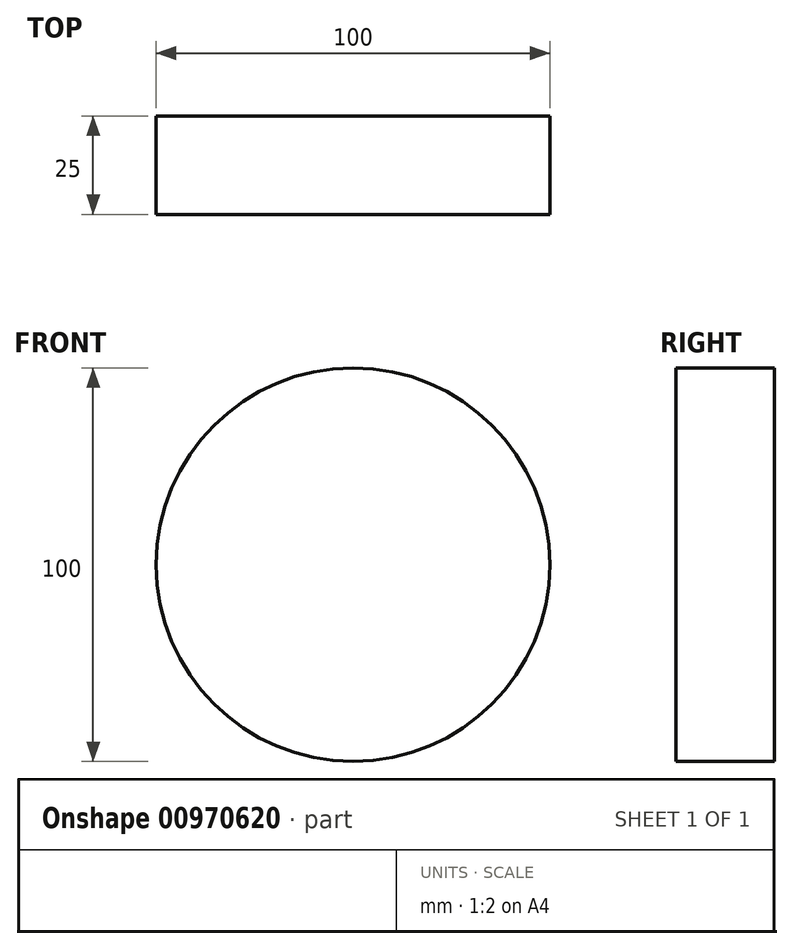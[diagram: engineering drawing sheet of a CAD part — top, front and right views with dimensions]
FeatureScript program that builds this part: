
annotation { "Feature Type Name" : "Feature", "Feature Type Description" : "" }
export const myFeature = defineFeature(function(context is Context, id is Id, definition is map)
    precondition{}
    {
        {
            var Q0;
            Q0=qCreatedBy(makeId("Front.planeOp"),FACE);
            var sketch = newSketch(context, id + "F0", { "sketchPlane" : qUnion([Q0])});
            skCircle(sketch, "E0", {"center": v(0, 0) * mm, "radius": 50 * mm});
            skLineSegment(sketch, "E1", {"start": v(-6.23, 49.61) * mm, "end": v(-1.88, 59.39) * mm});
            skLineSegment(sketch, "E2", {"start": v(-1.88, 59.39) * mm, "end": v(2.2, 59.39) * mm});
            skLineSegment(sketch, "E3", {"start": v(2.2, 59.39) * mm, "end": v(6.5, 49.57) * mm});
            skLineSegment(sketch, "E4.1.0", {"start": v(-22.08, 55.17) * mm, "end": v(-18.24, 56.56) * mm});
            skLineSegment(sketch, "E4.1.1", {"start": v(-18.24, 56.56) * mm, "end": v(-10.84, 48.81) * mm});
            skLineSegment(sketch, "E4.1.2", {"start": v(-22.82, 44.49) * mm, "end": v(-22.08, 55.17) * mm});
            skLineSegment(sketch, "E4.2.0", {"start": v(-39.61, 44.29) * mm, "end": v(-36.49, 46.91) * mm});
            skLineSegment(sketch, "E4.2.1", {"start": v(-36.49, 46.91) * mm, "end": v(-26.88, 42.16) * mm});
            skLineSegment(sketch, "E4.2.2", {"start": v(-36.66, 34) * mm, "end": v(-39.61, 44.29) * mm});
            skLineSegment(sketch, "E4.3.0", {"start": v(-52.37, 28.07) * mm, "end": v(-50.33, 31.6) * mm});
            skLineSegment(sketch, "E4.3.1", {"start": v(-50.33, 31.6) * mm, "end": v(-39.68, 30.42) * mm});
            skLineSegment(sketch, "E4.3.2", {"start": v(-46.08, 19.41) * mm, "end": v(-52.37, 28.07) * mm});
            skLineSegment(sketch, "E4.4.0", {"start": v(-58.81, 8.46) * mm, "end": v(-58.1, 12.48) * mm});
            skLineSegment(sketch, "E4.4.1", {"start": v(-58.1, 12.48) * mm, "end": v(-47.7, 15.02) * mm});
            skLineSegment(sketch, "E4.4.2", {"start": v(-49.94, 2.48) * mm, "end": v(-58.81, 8.46) * mm});
            skLineSegment(sketch, "E4.5.0", {"start": v(-58.16, -12.16) * mm, "end": v(-58.87, -8.14) * mm});
            skLineSegment(sketch, "E4.5.1", {"start": v(-58.87, -8.14) * mm, "end": v(-49.95, -2.2) * mm});
            skLineSegment(sketch, "E4.5.2", {"start": v(-47.78, -14.75) * mm, "end": v(-58.16, -12.16) * mm});
            skLineSegment(sketch, "E4.6.0", {"start": v(-50.5, -31.32) * mm, "end": v(-52.54, -27.78) * mm});
            skLineSegment(sketch, "E4.6.1", {"start": v(-52.54, -27.78) * mm, "end": v(-46.19, -19.15) * mm});
            skLineSegment(sketch, "E4.6.2", {"start": v(-39.85, -30.2) * mm, "end": v(-50.5, -31.32) * mm});
            skLineSegment(sketch, "E4.7.0", {"start": v(-36.74, -46.7) * mm, "end": v(-39.86, -44.08) * mm});
            skLineSegment(sketch, "E4.7.1", {"start": v(-39.86, -44.08) * mm, "end": v(-36.85, -33.8) * mm});
            skLineSegment(sketch, "E4.7.2", {"start": v(-27.12, -42) * mm, "end": v(-36.74, -46.7) * mm});
            skLineSegment(sketch, "E4.8.0", {"start": v(-18.55, -56.45) * mm, "end": v(-22.38, -55.05) * mm});
            skLineSegment(sketch, "E4.8.1", {"start": v(-22.38, -55.05) * mm, "end": v(-23.07, -44.36) * mm});
            skLineSegment(sketch, "E4.8.2", {"start": v(-11.11, -48.75) * mm, "end": v(-18.55, -56.45) * mm});
            skLineSegment(sketch, "E4.9.0", {"start": v(1.88, -59.39) * mm, "end": v(-2.2, -59.39) * mm});
            skLineSegment(sketch, "E4.9.1", {"start": v(-2.2, -59.39) * mm, "end": v(-6.5, -49.57) * mm});
            skLineSegment(sketch, "E4.9.2", {"start": v(6.23, -49.61) * mm, "end": v(1.88, -59.39) * mm});
            skLineSegment(sketch, "E4.10.0", {"start": v(22.08, -55.17) * mm, "end": v(18.24, -56.56) * mm});
            skLineSegment(sketch, "E4.10.1", {"start": v(18.24, -56.56) * mm, "end": v(10.84, -48.81) * mm});
            skLineSegment(sketch, "E4.10.2", {"start": v(22.82, -44.49) * mm, "end": v(22.08, -55.17) * mm});
            skLineSegment(sketch, "E4.11.0", {"start": v(39.61, -44.29) * mm, "end": v(36.49, -46.91) * mm});
            skLineSegment(sketch, "E4.11.1", {"start": v(36.49, -46.91) * mm, "end": v(26.88, -42.16) * mm});
            skLineSegment(sketch, "E4.11.2", {"start": v(36.66, -34) * mm, "end": v(39.61, -44.29) * mm});
            skLineSegment(sketch, "E4.12.0", {"start": v(52.37, -28.07) * mm, "end": v(50.33, -31.6) * mm});
            skLineSegment(sketch, "E4.12.1", {"start": v(50.33, -31.6) * mm, "end": v(39.68, -30.42) * mm});
            skLineSegment(sketch, "E4.12.2", {"start": v(46.08, -19.41) * mm, "end": v(52.37, -28.07) * mm});
            skLineSegment(sketch, "E4.13.0", {"start": v(58.81, -8.46) * mm, "end": v(58.1, -12.48) * mm});
            skLineSegment(sketch, "E4.13.1", {"start": v(58.1, -12.48) * mm, "end": v(47.7, -15.02) * mm});
            skLineSegment(sketch, "E4.13.2", {"start": v(49.94, -2.48) * mm, "end": v(58.81, -8.46) * mm});
            skLineSegment(sketch, "E4.14.0", {"start": v(58.16, 12.16) * mm, "end": v(58.87, 8.14) * mm});
            skLineSegment(sketch, "E4.14.1", {"start": v(58.87, 8.14) * mm, "end": v(49.95, 2.2) * mm});
            skLineSegment(sketch, "E4.14.2", {"start": v(47.78, 14.75) * mm, "end": v(58.16, 12.16) * mm});
            skLineSegment(sketch, "E4.15.0", {"start": v(50.5, 31.32) * mm, "end": v(52.54, 27.78) * mm});
            skLineSegment(sketch, "E4.15.1", {"start": v(52.54, 27.78) * mm, "end": v(46.19, 19.15) * mm});
            skLineSegment(sketch, "E4.15.2", {"start": v(39.85, 30.2) * mm, "end": v(50.5, 31.32) * mm});
            skLineSegment(sketch, "E4.16.0", {"start": v(36.74, 46.7) * mm, "end": v(39.86, 44.08) * mm});
            skLineSegment(sketch, "E4.16.1", {"start": v(39.86, 44.08) * mm, "end": v(36.85, 33.8) * mm});
            skLineSegment(sketch, "E4.16.2", {"start": v(27.12, 42) * mm, "end": v(36.74, 46.7) * mm});
            skLineSegment(sketch, "E4.17.0", {"start": v(18.55, 56.45) * mm, "end": v(22.38, 55.05) * mm});
            skLineSegment(sketch, "E4.17.1", {"start": v(22.38, 55.05) * mm, "end": v(23.07, 44.36) * mm});
            skLineSegment(sketch, "E4.17.2", {"start": v(11.11, 48.75) * mm, "end": v(18.55, 56.45) * mm});
            skSolve(sketch);
        }
        {
            var Q0;
            {var subQ0=sQuery(id+"F0.wireOp",EDGE,"E0");var subQ18=makeQuery(id+"F0.imprint","INTERSECT",VERTEX,{"derivedFrom":[subQ0,sQuery(id+"F0.wireOp",EDGE,"E4.14.1")]});Q0=makeQuery(id+"F0.imprint","IMPRINT",FACE,{"disambiguationData":[TD([[makeQuery(id+"F0.imprint","IMPRINT",EDGE,{"disambiguationData":[TD([[subQ18,-1.0]])],"derivedFrom":subQ0}),1.0]])]});}
            extrude(context, id + "F1", {"entities" : qUnion([Q0]), "oppositeDirection" : true, "depth" : 25 * mm, "offsetDistance" : 25 * mm});
        }
    });
